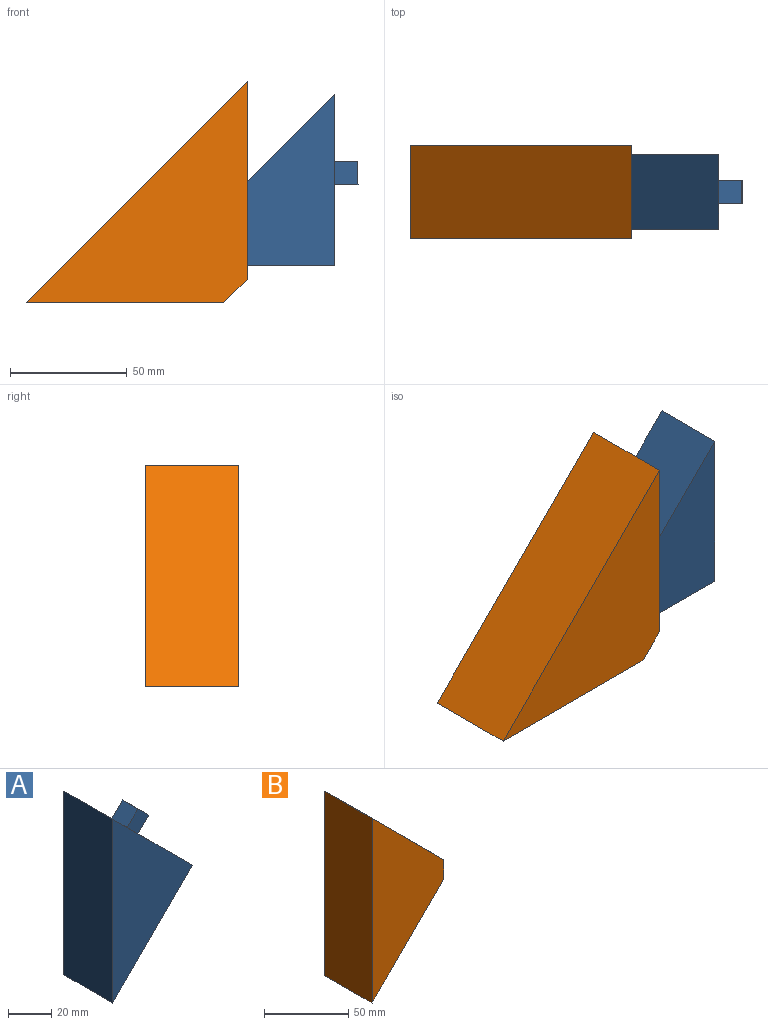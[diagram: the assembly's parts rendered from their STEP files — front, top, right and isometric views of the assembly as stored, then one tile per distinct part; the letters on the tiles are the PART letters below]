
ASSEMBLY  parts=2 mates=1
PART A: 10 faces, bbox 52x32x104 mm
  f0: plane 52x52mm, normal (0.71,0,0.71), area 2253.3mm2, adj f1,f2,f3,f4,f5,f6,f7,f8
  f1: plane 104x32mm, normal (-1,0,0), area 3328mm2, adj f0,f2,f3,f4
  f2: plane 104x52mm, normal (0,-1,0), area 2704mm2, adj f0,f1,f4
  f3: plane 104x52mm, normal (0,1,0), area 2704mm2, adj f0,f1,f4
  f4: plane 52x52mm, normal (0.71,0,-0.71), area 2353.3mm2, adj f0,f1,f2,f3
  f5: plane 10x7.07mm, normal (0.71,0,-0.71), area 100mm2, adj f0,f6,f8,f9
  f6: plane 14.14x14.14mm, normal (0,1,0), area 100mm2, adj f0,f5,f7,f9
  f7: plane 10x7.07mm, normal (-0.71,0,0.71), area 100mm2, adj f0,f6,f8,f9
  f8: plane 14.14x14.14mm, normal (0,-1,0), area 100mm2, adj f0,f5,f7,f9
  f9: plane 10x7.07mm, normal (0.71,0,0.71), area 100mm2, adj f5,f6,f7,f8
PART B: 10 faces, bbox 60x40x134.1 mm
  f0: plane 126.14x52mm, normal (0,-1,0), area 3855.4mm2, adj f1,f3,f4,f5
  f1: plane 126.14x32mm, normal (1,0,0), area 4036.5mm2, adj f0,f2,f4,f5
  f2: plane 126.14x52mm, normal (0,1,0), area 3855.4mm2, adj f1,f3,f4,f5
  f3: plane 32x22.14mm, normal (-1,0,0), area 708.5mm2, adj f0,f2,f4,f5
  f4: plane 60x60mm, normal (0.71,0,0.71), area 1040.9mm2, adj f0,f1,f2,f3,f6,f7,f8,f9
  f5: plane 60x60mm, normal (0.71,0,-0.71), area 1040.9mm2, adj f0,f1,f2,f3,f6,f7,f8,f9
  f6: plane 134.14x60mm, normal (0,-1,0), area 4448.5mm2, adj f4,f5,f7,f9
  f7: plane 40x14.14mm, normal (1,0,0), area 565.7mm2, adj f4,f5,f6,f8
  f8: plane 134.14x60mm, normal (0,1,0), area 4448.5mm2, adj f4,f5,f7,f9
  f9: plane 134.14x40mm, normal (-1,0,0), area 5365.7mm2, adj f4,f5,f6,f8
PLACE A rot(axis=(0,1,0),45deg) t=(61.62,0,-12.6)mm
PLACE B rot(axis=(0,1,0),45deg) t=(15.56,0,-21.21)mm
MATE slider A.f0 <-> B.f4  axis (1,0,0) through (126.77,0,52.43)mm
